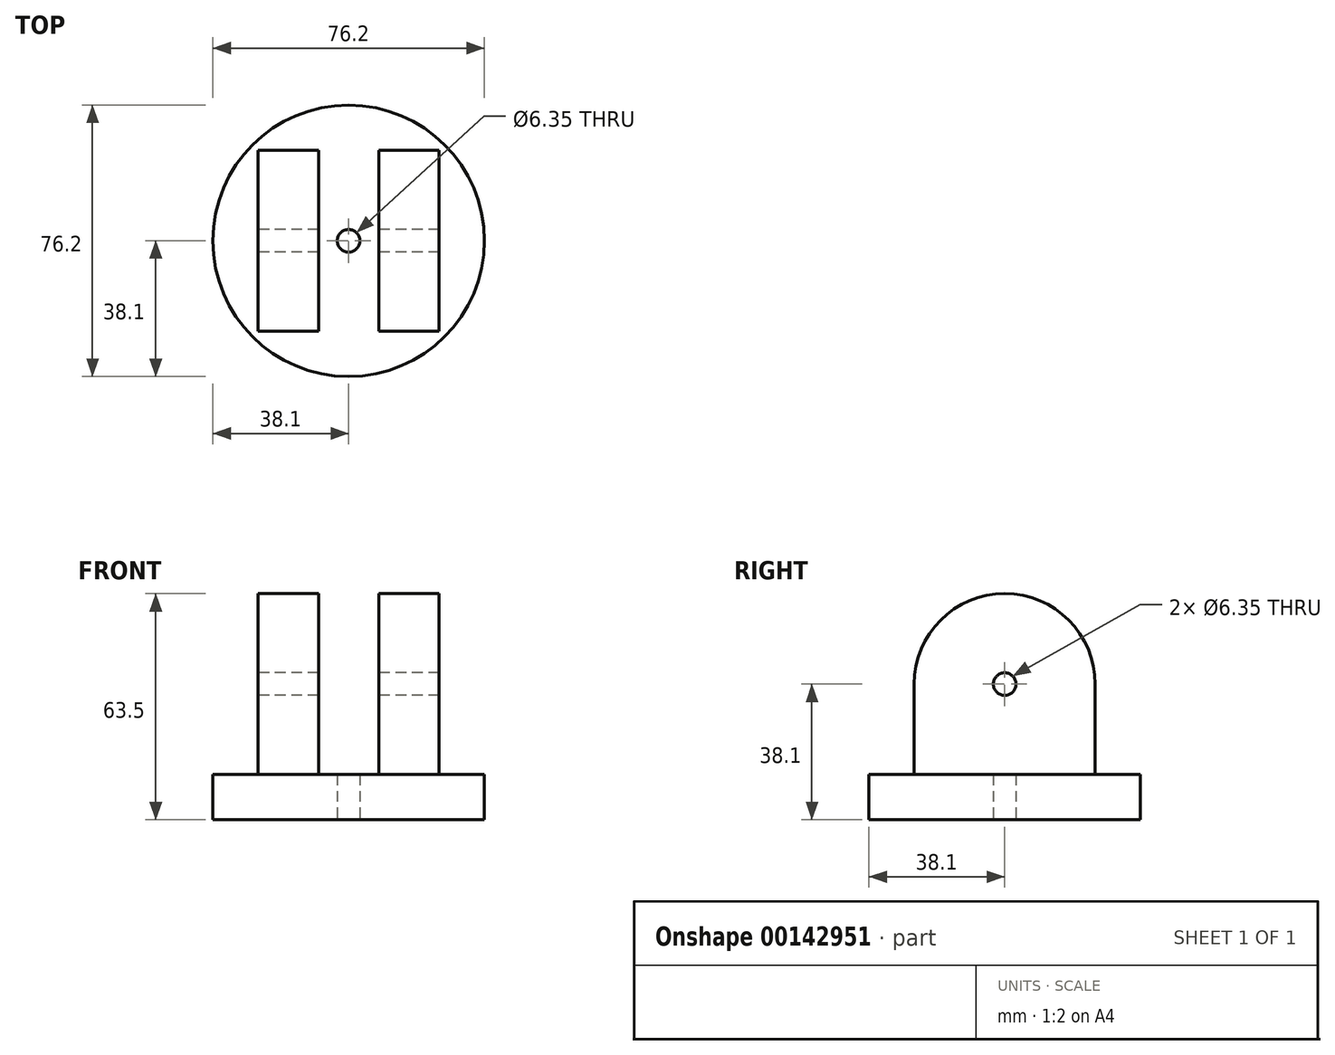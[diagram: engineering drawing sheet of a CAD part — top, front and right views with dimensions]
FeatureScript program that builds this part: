
annotation { "Feature Type Name" : "Feature", "Feature Type Description" : "" }
export const myFeature = defineFeature(function(context is Context, id is Id, definition is map)
    precondition{}
    {
        {
            var Q0;
            Q0=qCreatedBy(makeId("Top.planeOp"),FACE);
            var sketch = newSketch(context, id + "F0", { "sketchPlane" : qUnion([Q0])});
            skCircle(sketch, "E0", {"center": v(0, 0) * mm, "radius": 38.1 * mm});
            skCircle(sketch, "E1", {"center": v(0, 0) * mm, "radius": 3.18 * mm});
            skSolve(sketch);
        }
        {
            var Q0;
            Q0=makeQuery(id+"F0.imprint","IMPRINT",FACE,{"disambiguationData":[TD([[makeQuery(id+"F0.imprint","IMPRINT",EDGE,{"derivedFrom":sQuery(id+"F0.wireOp",EDGE,"E1")}),1.0]])]});
            extrude(context, id + "F1", {"entities" : qUnion([Q0]), "oppositeDirection" : true, "depth" : 25.4 * mm});
        }
        {
            var Q0;
            Q0=makeQuery(id+"F0.imprint","IMPRINT",FACE,{"disambiguationData":[TD([[makeQuery(id+"F0.imprint","IMPRINT",EDGE,{"derivedFrom":sQuery(id+"F0.wireOp",EDGE,"E0")}),1.0]])]});
            var Q1;
            Q1=makeQuery(id+"F0.imprint","IMPRINT",FACE,{"disambiguationData":[TD([[makeQuery(id+"F0.imprint","IMPRINT",EDGE,{"derivedFrom":sQuery(id+"F0.wireOp",EDGE,"E1")}),1.0]])]});
            extrude(context, id + "F2", {"entities" : qUnion([Q0, Q1]), "operationType" : NewBodyOperationType.ADD, "depth" : 12.7 * mm});
        }
        {
            var Q0;
            Q0=makeQuery(id+"F2.opExtrude","CAP_FACE",FACE,{"disambiguationData":[OSD([sQuery(id+"F0.wireOp",EDGE,"E0")])],"isStart":false});
            var sketch = newSketch(context, id + "F3", { "sketchPlane" : qUnion([Q0])});
            skLineSegment(sketch, "E2.bottom", {"start": v(-25.4, -25.4) * mm, "end": v(25.4, -25.4) * mm});
            skLineSegment(sketch, "E2.top", {"start": v(-25.4, 25.4) * mm, "end": v(25.4, 25.4) * mm});
            skLineSegment(sketch, "E2.left", {"start": v(-25.4, -25.4) * mm, "end": v(-25.4, 25.4) * mm});
            skLineSegment(sketch, "E2.right", {"start": v(25.4, -25.4) * mm, "end": v(25.4, 25.4) * mm});
            skLineSegment(sketch, "E3", {"start": v(-8.47, 25.4) * mm, "end": v(-8.47, -25.4) * mm});
            skLineSegment(sketch, "E4", {"start": v(8.47, 25.4) * mm, "end": v(8.47, -25.4) * mm});
            skSolve(sketch);
        }
        {
            var Q0;
            {var subQ0=sQuery(id+"F3.wireOp",EDGE,"E2.right");Q0=makeQuery(id+"F3.imprint","IMPRINT",FACE,{"disambiguationData":[TD([[makeQuery(id+"F3.imprint","IMPRINT",EDGE,{"derivedFrom":subQ0}),1.0]])]});}
            var Q1;
            {var subQ0=sQuery(id+"F3.wireOp",EDGE,"E2.left");Q1=makeQuery(id+"F3.imprint","IMPRINT",FACE,{"disambiguationData":[TD([[makeQuery(id+"F3.imprint","IMPRINT",EDGE,{"derivedFrom":subQ0}),-1.0]])]});}
            extrude(context, id + "F4", {"entities" : qUnion([Q0, Q1]), "operationType" : NewBodyOperationType.ADD, "depth" : 50.8 * mm});
        }
        {
            var Q0;
            {var subQ0=sQuery(id+"F3.wireOp",EDGE,"E2.bottom");Q0=makeQuery(id+"F4.opExtrude","CAP_EDGE",EDGE,{"disambiguationData":[OSD([subQ0]),TDD([makeQuery(id+"F3.imprint","IMPRINT",EDGE,{"disambiguationData":[TD([[makeQuery(id+"F3.imprint","INTERSECT",VERTEX,{"derivedFrom":[subQ0,sQuery(id+"F3.wireOp",EDGE,"E2.right")]}),1.0]])],"derivedFrom":subQ0})])],"isStart":false});}
            var Q1;
            {var subQ0=sQuery(id+"F3.wireOp",EDGE,"E2.top");Q1=makeQuery(id+"F4.opExtrude","CAP_EDGE",EDGE,{"disambiguationData":[OSD([subQ0]),TDD([makeQuery(id+"F3.imprint","IMPRINT",EDGE,{"disambiguationData":[TD([[makeQuery(id+"F3.imprint","INTERSECT",VERTEX,{"derivedFrom":[subQ0,sQuery(id+"F3.wireOp",EDGE,"E2.right")]}),1.0]])],"derivedFrom":subQ0})])],"isStart":false});}
            var Q2;
            {var subQ0=sQuery(id+"F3.wireOp",EDGE,"E2.top");Q2=makeQuery(id+"F4.opExtrude","CAP_EDGE",EDGE,{"disambiguationData":[OSD([subQ0]),TDD([makeQuery(id+"F3.imprint","IMPRINT",EDGE,{"disambiguationData":[TD([[makeQuery(id+"F3.imprint","INTERSECT",VERTEX,{"derivedFrom":[subQ0,sQuery(id+"F3.wireOp",EDGE,"E2.left")]}),-1.0]])],"derivedFrom":subQ0})])],"isStart":false});}
            var Q3;
            {var subQ0=sQuery(id+"F3.wireOp",EDGE,"E2.bottom");Q3=makeQuery(id+"F4.opExtrude","CAP_EDGE",EDGE,{"disambiguationData":[OSD([subQ0]),TDD([makeQuery(id+"F3.imprint","IMPRINT",EDGE,{"disambiguationData":[TD([[makeQuery(id+"F3.imprint","INTERSECT",VERTEX,{"derivedFrom":[subQ0,sQuery(id+"F3.wireOp",EDGE,"E2.left")]}),-1.0]])],"derivedFrom":subQ0})])],"isStart":false});}
            fillet(context, id + "F5", {"entities" : qUnion([Q0, Q1, Q2, Q3]), "radius" : 25.4 * mm, "tangentPropagation" : true, "allowEdgeOverflow" : false});
        }
        {
            var Q0;
            Q0=makeQuery(id+"F4.opExtrude","SWEPT_FACE",FACE,{"disambiguationData":[OSD([sQuery(id+"F3.wireOp",EDGE,"E2.left")])]});
            var sketch = newSketch(context, id + "F6", { "sketchPlane" : qUnion([Q0])});
            skCircle(sketch, "E5", {"center": v(0, 38.1) * mm, "radius": 3.18 * mm});
            skSolve(sketch);
        }
        {
            var Q0;
            Q0=makeQuery(id+"F6.imprint","IMPRINT",FACE,{"disambiguationData":[TD([[makeQuery(id+"F6.imprint","IMPRINT",EDGE,{"derivedFrom":sQuery(id+"F6.wireOp",EDGE,"E5")}),1.0]])]});
            extrude(context, id + "F7", {"entities" : qUnion([Q0]), "operationType" : NewBodyOperationType.REMOVE, "oppositeDirection" : true, "depth" : 103.24 * mm});
        }
        {
            var Q0;
            Q0=makeQuery(id+"F1.opExtrude","CAP_FACE",FACE,{"disambiguationData":[OSD([sQuery(id+"F0.wireOp",EDGE,"E1")])],"isStart":false});
            extrude(context, id + "F8", {"entities" : qUnion([Q0]), "operationType" : NewBodyOperationType.REMOVE, "oppositeDirection" : true, "depth" : 120.65 * mm});
        }
    });
